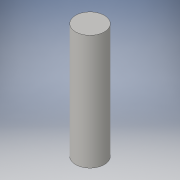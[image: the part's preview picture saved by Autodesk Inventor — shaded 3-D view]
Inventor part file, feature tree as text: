
AUTODESK INVENTOR PART (.ipt)
format: ipt  version: 2016 (Build 200138000, 138)  size: 84,480 bytes
history: native  units: in
note: dims shown in document units (in); Inventor stores cm internally (conversion verified against a paired STEP export)
features: extrude x1, sketch x1
ambient origin geometry x8: Origin, YZ Plane, XZ Plane, XY Plane, X Axis, Y Axis, Z Axis, Center Point
bodies: Solid1 (feature_tree)
feature tree (2):
  extrude  "Extrusion1"  Depth=1.5748in TaperAngle=0.0deg
  sketch  "Sketch1"  dims[d0=0.3937in d1=1.5748in d2=0.0in]
